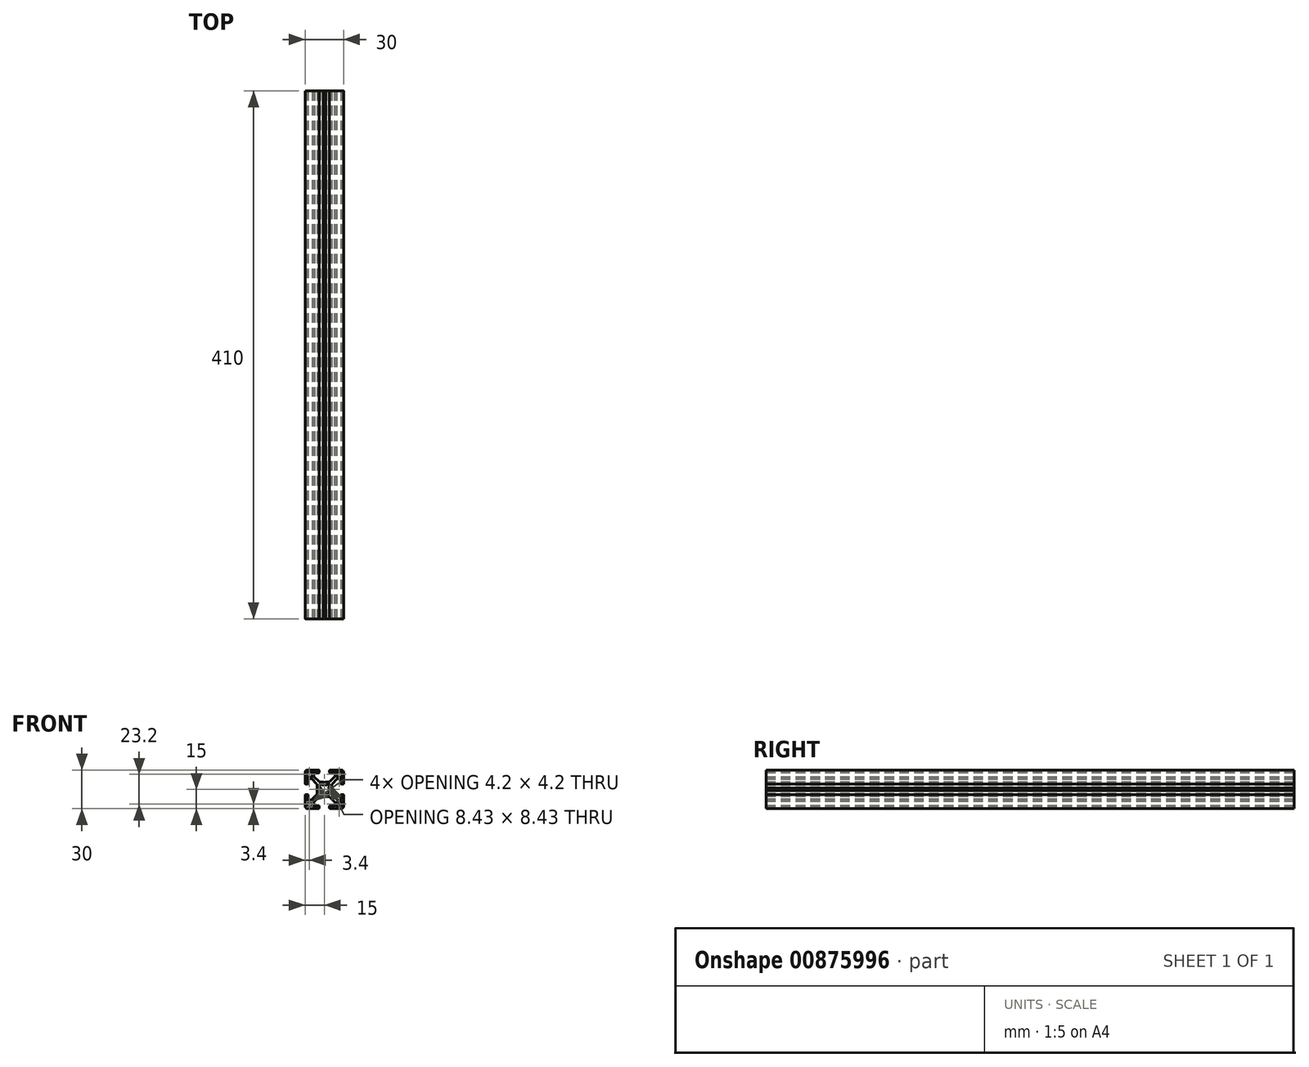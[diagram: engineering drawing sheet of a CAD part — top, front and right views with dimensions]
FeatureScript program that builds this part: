
annotation { "Feature Type Name" : "Feature", "Feature Type Description" : "" }
export const myFeature = defineFeature(function(context is Context, id is Id, definition is map)
    precondition{}
    {
        {
            var Q0;
            Q0=qCreatedBy(makeId("Front.planeOp"),FACE);
            var sketch = newSketch(context, id + "F0", { "sketchPlane" : qUnion([Q0])});
            skArc(sketch, "E0", {"start": v(9.88, 13.7) * mm, "mid": v(9.61, 13.59) * mm, "end": v(9.5, 13.32) * mm});
            skLineSegment(sketch, "E1", {"start": v(12.7, 13.7) * mm, "end": v(9.88, 13.7) * mm});
            skArc(sketch, "E2", {"start": v(13.7, 12.7) * mm, "mid": v(13.4, 13.4) * mm, "end": v(12.7, 13.7) * mm});
            skLineSegment(sketch, "E3", {"start": v(13.7, 9.88) * mm, "end": v(13.7, 12.7) * mm});
            skArc(sketch, "E4", {"start": v(13.32, 9.5) * mm, "mid": v(13.59, 9.61) * mm, "end": v(13.7, 9.88) * mm});
            skLineSegment(sketch, "E5", {"start": v(9.88, 9.5) * mm, "end": v(13.32, 9.5) * mm});
            skArc(sketch, "E6", {"start": v(9.5, 9.88) * mm, "mid": v(9.61, 9.61) * mm, "end": v(9.88, 9.5) * mm});
            skLineSegment(sketch, "E7", {"start": v(9.5, 13.32) * mm, "end": v(9.5, 9.88) * mm});
            skArc(sketch, "E8", {"start": v(-9.5, 13.32) * mm, "mid": v(-9.61, 13.59) * mm, "end": v(-9.88, 13.7) * mm});
            skLineSegment(sketch, "E9", {"start": v(-9.5, 9.88) * mm, "end": v(-9.5, 13.32) * mm});
            skArc(sketch, "E10", {"start": v(-9.88, 9.5) * mm, "mid": v(-9.61, 9.61) * mm, "end": v(-9.5, 9.88) * mm});
            skLineSegment(sketch, "E11", {"start": v(-13.32, 9.5) * mm, "end": v(-9.88, 9.5) * mm});
            skArc(sketch, "E12", {"start": v(-13.7, 9.88) * mm, "mid": v(-13.59, 9.61) * mm, "end": v(-13.32, 9.5) * mm});
            skLineSegment(sketch, "E13", {"start": v(-13.7, 12.7) * mm, "end": v(-13.7, 9.88) * mm});
            skArc(sketch, "E14", {"start": v(-12.7, 13.7) * mm, "mid": v(-13.4, 13.4) * mm, "end": v(-13.7, 12.7) * mm});
            skLineSegment(sketch, "E15", {"start": v(-9.88, 13.7) * mm, "end": v(-12.7, 13.7) * mm});
            skArc(sketch, "E16", {"start": v(-1.5, -3.2) * mm, "mid": v(0, -3.53) * mm, "end": v(1.5, -3.2) * mm});
            skLineSegment(sketch, "E17", {"start": v(-2.47, -3.98) * mm, "end": v(-1.5, -3.2) * mm});
            skArc(sketch, "E18", {"start": v(-3.98, -2.47) * mm, "mid": v(-3.9, -3.9) * mm, "end": v(-2.47, -3.98) * mm});
            skLineSegment(sketch, "E19", {"start": v(-3.2, -1.5) * mm, "end": v(-3.98, -2.47) * mm});
            skArc(sketch, "E20", {"start": v(-3.2, 1.5) * mm, "mid": v(-3.53, 0) * mm, "end": v(-3.2, -1.5) * mm});
            skLineSegment(sketch, "E21", {"start": v(-3.98, 2.47) * mm, "end": v(-3.2, 1.5) * mm});
            skArc(sketch, "E22", {"start": v(-2.47, 3.98) * mm, "mid": v(-3.9, 3.9) * mm, "end": v(-3.98, 2.47) * mm});
            skLineSegment(sketch, "E23", {"start": v(-1.5, 3.2) * mm, "end": v(-2.47, 3.98) * mm});
            skArc(sketch, "E24", {"start": v(1.5, 3.2) * mm, "mid": v(0, 3.53) * mm, "end": v(-1.5, 3.2) * mm});
            skLineSegment(sketch, "E25", {"start": v(2.47, 3.98) * mm, "end": v(1.5, 3.2) * mm});
            skArc(sketch, "E26", {"start": v(3.98, 2.47) * mm, "mid": v(3.9, 3.9) * mm, "end": v(2.47, 3.98) * mm});
            skLineSegment(sketch, "E27", {"start": v(3.2, 1.5) * mm, "end": v(3.98, 2.47) * mm});
            skArc(sketch, "E28", {"start": v(3.2, -1.5) * mm, "mid": v(3.53, 0) * mm, "end": v(3.2, 1.5) * mm});
            skLineSegment(sketch, "E29", {"start": v(3.98, -2.47) * mm, "end": v(3.2, -1.5) * mm});
            skArc(sketch, "E30", {"start": v(2.47, -3.98) * mm, "mid": v(3.9, -3.9) * mm, "end": v(3.98, -2.47) * mm});
            skLineSegment(sketch, "E31", {"start": v(1.5, -3.2) * mm, "end": v(2.47, -3.98) * mm});
            skArc(sketch, "E32", {"start": v(-13.32, -9.5) * mm, "mid": v(-13.59, -9.61) * mm, "end": v(-13.7, -9.88) * mm});
            skLineSegment(sketch, "E33", {"start": v(-9.88, -9.5) * mm, "end": v(-13.32, -9.5) * mm});
            skArc(sketch, "E34", {"start": v(-9.5, -9.88) * mm, "mid": v(-9.61, -9.61) * mm, "end": v(-9.88, -9.5) * mm});
            skLineSegment(sketch, "E35", {"start": v(-9.5, -13.32) * mm, "end": v(-9.5, -9.88) * mm});
            skArc(sketch, "E36", {"start": v(-9.88, -13.7) * mm, "mid": v(-9.61, -13.59) * mm, "end": v(-9.5, -13.32) * mm});
            skLineSegment(sketch, "E37", {"start": v(-12.7, -13.7) * mm, "end": v(-9.88, -13.7) * mm});
            skArc(sketch, "E38", {"start": v(-13.7, -12.7) * mm, "mid": v(-13.4, -13.4) * mm, "end": v(-12.7, -13.7) * mm});
            skLineSegment(sketch, "E39", {"start": v(-13.7, -9.88) * mm, "end": v(-13.7, -12.7) * mm});
            skArc(sketch, "E40", {"start": v(9.5, -13.32) * mm, "mid": v(9.61, -13.59) * mm, "end": v(9.88, -13.7) * mm});
            skLineSegment(sketch, "E41", {"start": v(9.5, -9.88) * mm, "end": v(9.5, -13.32) * mm});
            skArc(sketch, "E42", {"start": v(9.88, -9.5) * mm, "mid": v(9.61, -9.61) * mm, "end": v(9.5, -9.88) * mm});
            skLineSegment(sketch, "E43", {"start": v(13.32, -9.5) * mm, "end": v(9.88, -9.5) * mm});
            skArc(sketch, "E44", {"start": v(13.7, -9.88) * mm, "mid": v(13.59, -9.61) * mm, "end": v(13.32, -9.5) * mm});
            skLineSegment(sketch, "E45", {"start": v(13.7, -12.7) * mm, "end": v(13.7, -9.88) * mm});
            skArc(sketch, "E46", {"start": v(12.7, -13.7) * mm, "mid": v(13.4, -13.4) * mm, "end": v(13.7, -12.7) * mm});
            skLineSegment(sketch, "E47", {"start": v(9.88, -13.7) * mm, "end": v(12.7, -13.7) * mm});
            skArc(sketch, "E48", {"start": v(13.24, -4) * mm, "mid": v(12.89, -4.15) * mm, "end": v(12.74, -4.5) * mm});
            skLineSegment(sketch, "E49", {"start": v(12.74, -4.5) * mm, "end": v(12.74, -7.73) * mm});
            skArc(sketch, "E50", {"start": v(12.24, -8.25) * mm, "mid": v(12.6, -8.1) * mm, "end": v(12.74, -7.73) * mm});
            skLineSegment(sketch, "E51", {"start": v(12.24, -8.25) * mm, "end": v(10.26, -8.25) * mm});
            skArc(sketch, "E52", {"start": v(9.9, -8.1) * mm, "mid": v(10.07, -8.21) * mm, "end": v(10.26, -8.25) * mm});
            skLineSegment(sketch, "E53", {"start": v(9.9, -8.1) * mm, "end": v(5.98, -4.18) * mm});
            skArc(sketch, "E54", {"start": v(5.83, -3.82) * mm, "mid": v(5.87, -4.02) * mm, "end": v(5.98, -4.18) * mm});
            skLineSegment(sketch, "E55", {"start": v(5.83, -3.82) * mm, "end": v(5.83, -1.01) * mm});
            skLineSegment(sketch, "E56", {"start": v(5.83, -1.01) * mm, "end": v(5.32, -0.06) * mm});
            skLineSegment(sketch, "E57", {"start": v(5.32, -0.06) * mm, "end": v(5.83, 0.89) * mm});
            skLineSegment(sketch, "E58", {"start": v(5.83, 0.89) * mm, "end": v(5.83, 3.82) * mm});
            skArc(sketch, "E59", {"start": v(5.98, 4.18) * mm, "mid": v(5.87, 4.02) * mm, "end": v(5.83, 3.82) * mm});
            skLineSegment(sketch, "E60", {"start": v(5.98, 4.18) * mm, "end": v(9.9, 8.1) * mm});
            skArc(sketch, "E61", {"start": v(10.26, 8.25) * mm, "mid": v(10.07, 8.21) * mm, "end": v(9.9, 8.1) * mm});
            skLineSegment(sketch, "E62", {"start": v(10.26, 8.25) * mm, "end": v(12.24, 8.25) * mm});
            skArc(sketch, "E63", {"start": v(12.74, 7.73) * mm, "mid": v(12.6, 8.1) * mm, "end": v(12.24, 8.25) * mm});
            skLineSegment(sketch, "E64", {"start": v(12.74, 7.73) * mm, "end": v(12.74, 4.5) * mm});
            skArc(sketch, "E65", {"start": v(12.74, 4.5) * mm, "mid": v(12.89, 4.15) * mm, "end": v(13.24, 4) * mm});
            skLineSegment(sketch, "E66", {"start": v(13.24, 4) * mm, "end": v(14.5, 4) * mm});
            skArc(sketch, "E67", {"start": v(14.5, 4) * mm, "mid": v(14.85, 4.15) * mm, "end": v(15, 4.5) * mm});
            skLineSegment(sketch, "E68", {"start": v(15, 4.5) * mm, "end": v(15, 13) * mm});
            skArc(sketch, "E69", {"start": v(15, 13) * mm, "mid": v(14.41, 14.41) * mm, "end": v(13, 15) * mm});
            skLineSegment(sketch, "E70", {"start": v(13, 15) * mm, "end": v(4.5, 15) * mm});
            skArc(sketch, "E71", {"start": v(4.5, 15) * mm, "mid": v(4.15, 14.85) * mm, "end": v(4, 14.5) * mm});
            skLineSegment(sketch, "E72", {"start": v(4, 14.5) * mm, "end": v(4, 13.24) * mm});
            skArc(sketch, "E73", {"start": v(4, 13.24) * mm, "mid": v(4.15, 12.89) * mm, "end": v(4.5, 12.74) * mm});
            skLineSegment(sketch, "E74", {"start": v(4.5, 12.74) * mm, "end": v(7.73, 12.74) * mm});
            skArc(sketch, "E75", {"start": v(8.25, 12.24) * mm, "mid": v(8.1, 12.6) * mm, "end": v(7.73, 12.74) * mm});
            skLineSegment(sketch, "E76", {"start": v(8.25, 12.24) * mm, "end": v(8.25, 10.26) * mm});
            skArc(sketch, "E77", {"start": v(8.1, 9.9) * mm, "mid": v(8.21, 10.07) * mm, "end": v(8.25, 10.26) * mm});
            skLineSegment(sketch, "E78", {"start": v(8.1, 9.9) * mm, "end": v(4.18, 5.98) * mm});
            skArc(sketch, "E79", {"start": v(3.82, 5.83) * mm, "mid": v(4.02, 5.87) * mm, "end": v(4.18, 5.98) * mm});
            skLineSegment(sketch, "E80", {"start": v(3.82, 5.83) * mm, "end": v(0.95, 5.83) * mm});
            skLineSegment(sketch, "E81", {"start": v(0.95, 5.83) * mm, "end": v(0, 5.32) * mm});
            skLineSegment(sketch, "E82", {"start": v(0, 5.32) * mm, "end": v(-0.95, 5.83) * mm});
            skLineSegment(sketch, "E83", {"start": v(-0.95, 5.83) * mm, "end": v(-3.82, 5.83) * mm});
            skArc(sketch, "E84", {"start": v(-4.18, 5.98) * mm, "mid": v(-4.02, 5.87) * mm, "end": v(-3.82, 5.83) * mm});
            skLineSegment(sketch, "E85", {"start": v(-4.18, 5.98) * mm, "end": v(-8.1, 9.9) * mm});
            skArc(sketch, "E86", {"start": v(-8.25, 10.26) * mm, "mid": v(-8.21, 10.07) * mm, "end": v(-8.1, 9.9) * mm});
            skLineSegment(sketch, "E87", {"start": v(-8.25, 10.26) * mm, "end": v(-8.25, 12.24) * mm});
            skArc(sketch, "E88", {"start": v(-7.73, 12.74) * mm, "mid": v(-8.1, 12.6) * mm, "end": v(-8.25, 12.24) * mm});
            skLineSegment(sketch, "E89", {"start": v(-7.73, 12.74) * mm, "end": v(-4.5, 12.74) * mm});
            skArc(sketch, "E90", {"start": v(-4.5, 12.74) * mm, "mid": v(-4.15, 12.89) * mm, "end": v(-4, 13.24) * mm});
            skLineSegment(sketch, "E91", {"start": v(-4, 13.24) * mm, "end": v(-4, 14.5) * mm});
            skArc(sketch, "E92", {"start": v(-4, 14.5) * mm, "mid": v(-4.15, 14.85) * mm, "end": v(-4.5, 15) * mm});
            skLineSegment(sketch, "E93", {"start": v(-4.5, 15) * mm, "end": v(-13, 15) * mm});
            skArc(sketch, "E94", {"start": v(-13, 15) * mm, "mid": v(-14.41, 14.41) * mm, "end": v(-15, 13) * mm});
            skLineSegment(sketch, "E95", {"start": v(-15, 13) * mm, "end": v(-15, 4.5) * mm});
            skArc(sketch, "E96", {"start": v(-15, 4.5) * mm, "mid": v(-14.85, 4.15) * mm, "end": v(-14.5, 4) * mm});
            skLineSegment(sketch, "E97", {"start": v(-14.5, 4) * mm, "end": v(-13.24, 4) * mm});
            skArc(sketch, "E98", {"start": v(-13.24, 4) * mm, "mid": v(-12.89, 4.15) * mm, "end": v(-12.74, 4.5) * mm});
            skLineSegment(sketch, "E99", {"start": v(-12.74, 4.5) * mm, "end": v(-12.74, 7.73) * mm});
            skArc(sketch, "E100", {"start": v(-12.24, 8.25) * mm, "mid": v(-12.6, 8.1) * mm, "end": v(-12.74, 7.73) * mm});
            skLineSegment(sketch, "E101", {"start": v(-12.24, 8.25) * mm, "end": v(-10.26, 8.25) * mm});
            skArc(sketch, "E102", {"start": v(-9.9, 8.1) * mm, "mid": v(-10.07, 8.21) * mm, "end": v(-10.26, 8.25) * mm});
            skLineSegment(sketch, "E103", {"start": v(-9.9, 8.1) * mm, "end": v(-5.98, 4.18) * mm});
            skArc(sketch, "E104", {"start": v(-5.83, 3.82) * mm, "mid": v(-5.87, 4.02) * mm, "end": v(-5.98, 4.18) * mm});
            skLineSegment(sketch, "E105", {"start": v(-5.83, 3.82) * mm, "end": v(-5.83, 0.89) * mm});
            skLineSegment(sketch, "E106", {"start": v(-5.83, 0.89) * mm, "end": v(-5.32, -0.06) * mm});
            skLineSegment(sketch, "E107", {"start": v(-5.32, -0.06) * mm, "end": v(-5.83, -1.01) * mm});
            skLineSegment(sketch, "E108", {"start": v(-5.83, -1.01) * mm, "end": v(-5.83, -3.82) * mm});
            skArc(sketch, "E109", {"start": v(-5.98, -4.18) * mm, "mid": v(-5.87, -4.02) * mm, "end": v(-5.83, -3.82) * mm});
            skLineSegment(sketch, "E110", {"start": v(-5.98, -4.18) * mm, "end": v(-9.9, -8.1) * mm});
            skArc(sketch, "E111", {"start": v(-10.26, -8.25) * mm, "mid": v(-10.07, -8.21) * mm, "end": v(-9.9, -8.1) * mm});
            skLineSegment(sketch, "E112", {"start": v(-10.26, -8.25) * mm, "end": v(-12.24, -8.25) * mm});
            skArc(sketch, "E113", {"start": v(-12.74, -7.73) * mm, "mid": v(-12.6, -8.1) * mm, "end": v(-12.24, -8.25) * mm});
            skLineSegment(sketch, "E114", {"start": v(-12.74, -7.73) * mm, "end": v(-12.74, -4.5) * mm});
            skArc(sketch, "E115", {"start": v(-12.74, -4.5) * mm, "mid": v(-12.89, -4.15) * mm, "end": v(-13.24, -4) * mm});
            skLineSegment(sketch, "E116", {"start": v(-13.24, -4) * mm, "end": v(-14.5, -4) * mm});
            skArc(sketch, "E117", {"start": v(-14.5, -4) * mm, "mid": v(-14.85, -4.15) * mm, "end": v(-15, -4.5) * mm});
            skLineSegment(sketch, "E118", {"start": v(-15, -4.5) * mm, "end": v(-15, -13) * mm});
            skArc(sketch, "E119", {"start": v(-15, -13) * mm, "mid": v(-14.41, -14.41) * mm, "end": v(-13, -15) * mm});
            skLineSegment(sketch, "E120", {"start": v(-13, -15) * mm, "end": v(-4.5, -15) * mm});
            skArc(sketch, "E121", {"start": v(-4.5, -15) * mm, "mid": v(-4.15, -14.85) * mm, "end": v(-4, -14.5) * mm});
            skLineSegment(sketch, "E122", {"start": v(-4, -14.5) * mm, "end": v(-4, -13.24) * mm});
            skArc(sketch, "E123", {"start": v(-4, -13.24) * mm, "mid": v(-4.15, -12.89) * mm, "end": v(-4.5, -12.74) * mm});
            skLineSegment(sketch, "E124", {"start": v(-4.5, -12.74) * mm, "end": v(-7.73, -12.74) * mm});
            skArc(sketch, "E125", {"start": v(-8.25, -12.24) * mm, "mid": v(-8.1, -12.6) * mm, "end": v(-7.73, -12.74) * mm});
            skLineSegment(sketch, "E126", {"start": v(-8.25, -12.24) * mm, "end": v(-8.25, -10.26) * mm});
            skArc(sketch, "E127", {"start": v(-8.1, -9.9) * mm, "mid": v(-8.21, -10.07) * mm, "end": v(-8.25, -10.26) * mm});
            skLineSegment(sketch, "E128", {"start": v(-8.1, -9.9) * mm, "end": v(-4.18, -5.98) * mm});
            skArc(sketch, "E129", {"start": v(-3.82, -5.83) * mm, "mid": v(-4.02, -5.87) * mm, "end": v(-4.18, -5.98) * mm});
            skLineSegment(sketch, "E130", {"start": v(-3.82, -5.83) * mm, "end": v(-0.95, -5.83) * mm});
            skLineSegment(sketch, "E131", {"start": v(-0.95, -5.83) * mm, "end": v(0, -5.32) * mm});
            skLineSegment(sketch, "E132", {"start": v(0, -5.32) * mm, "end": v(0.95, -5.83) * mm});
            skLineSegment(sketch, "E133", {"start": v(0.95, -5.83) * mm, "end": v(3.82, -5.83) * mm});
            skArc(sketch, "E134", {"start": v(4.18, -5.98) * mm, "mid": v(4.02, -5.87) * mm, "end": v(3.82, -5.83) * mm});
            skLineSegment(sketch, "E135", {"start": v(4.18, -5.98) * mm, "end": v(8.1, -9.9) * mm});
            skArc(sketch, "E136", {"start": v(8.25, -10.26) * mm, "mid": v(8.21, -10.07) * mm, "end": v(8.1, -9.9) * mm});
            skLineSegment(sketch, "E137", {"start": v(8.25, -10.26) * mm, "end": v(8.25, -12.24) * mm});
            skArc(sketch, "E138", {"start": v(7.73, -12.74) * mm, "mid": v(8.1, -12.6) * mm, "end": v(8.25, -12.24) * mm});
            skLineSegment(sketch, "E139", {"start": v(7.73, -12.74) * mm, "end": v(4.5, -12.74) * mm});
            skArc(sketch, "E140", {"start": v(4.5, -12.74) * mm, "mid": v(4.15, -12.89) * mm, "end": v(4, -13.24) * mm});
            skLineSegment(sketch, "E141", {"start": v(4, -13.24) * mm, "end": v(4, -14.5) * mm});
            skArc(sketch, "E142", {"start": v(4, -14.5) * mm, "mid": v(4.15, -14.85) * mm, "end": v(4.5, -15) * mm});
            skLineSegment(sketch, "E143", {"start": v(4.5, -15) * mm, "end": v(13, -15) * mm});
            skArc(sketch, "E144", {"start": v(13, -15) * mm, "mid": v(14.41, -14.41) * mm, "end": v(15, -13) * mm});
            skLineSegment(sketch, "E145", {"start": v(15, -13) * mm, "end": v(15, -4.5) * mm});
            skArc(sketch, "E146", {"start": v(15, -4.5) * mm, "mid": v(14.85, -4.15) * mm, "end": v(14.5, -4) * mm});
            skLineSegment(sketch, "E147", {"start": v(14.5, -4) * mm, "end": v(13.24, -4) * mm});
            skSolve(sketch);
        }
        {
            var Q0;
            Q0=qCreatedBy(makeId("Top.planeOp"),FACE);
            var sketch = newSketch(context, id + "F1", { "sketchPlane" : qUnion([Q0])});
            skLineSegment(sketch, "E148", {"start": v(-1.5, 205) * mm, "end": v(-1.5, -205) * mm});
            skSolve(sketch);
        }
        {
            var Q0;
            Q0=qSketchRegion(id+"F0",true);
            var Q1;
            Q1=sQuery(id+"F1.wireOp",EDGE,"E148");
            var Q2;
            Q2=sQuery(id+"F1.wireOp",EDGE,"fSjTIPXa-SZZ6-Uh3d-dTjF-iSAX6K3vTkU0");
            var Q3;
            Q3=sQuery(id+"F1.wireOp",EDGE,"X1iaMUp9-18Uv-Qplb-D4Eo-NhRo6oMLb04g");
            var Q4;
            Q4=sQuery(id+"F1.wireOp",EDGE,"ysMRVMGi-oqtn-a0SZ-pmm6-otZbrj3hBrry");
            sweep(context, id + "F2", {"profiles" : qUnion([Q0]), "path" : qUnion([Q1, Q2, Q3, Q4])});
        }
    });
